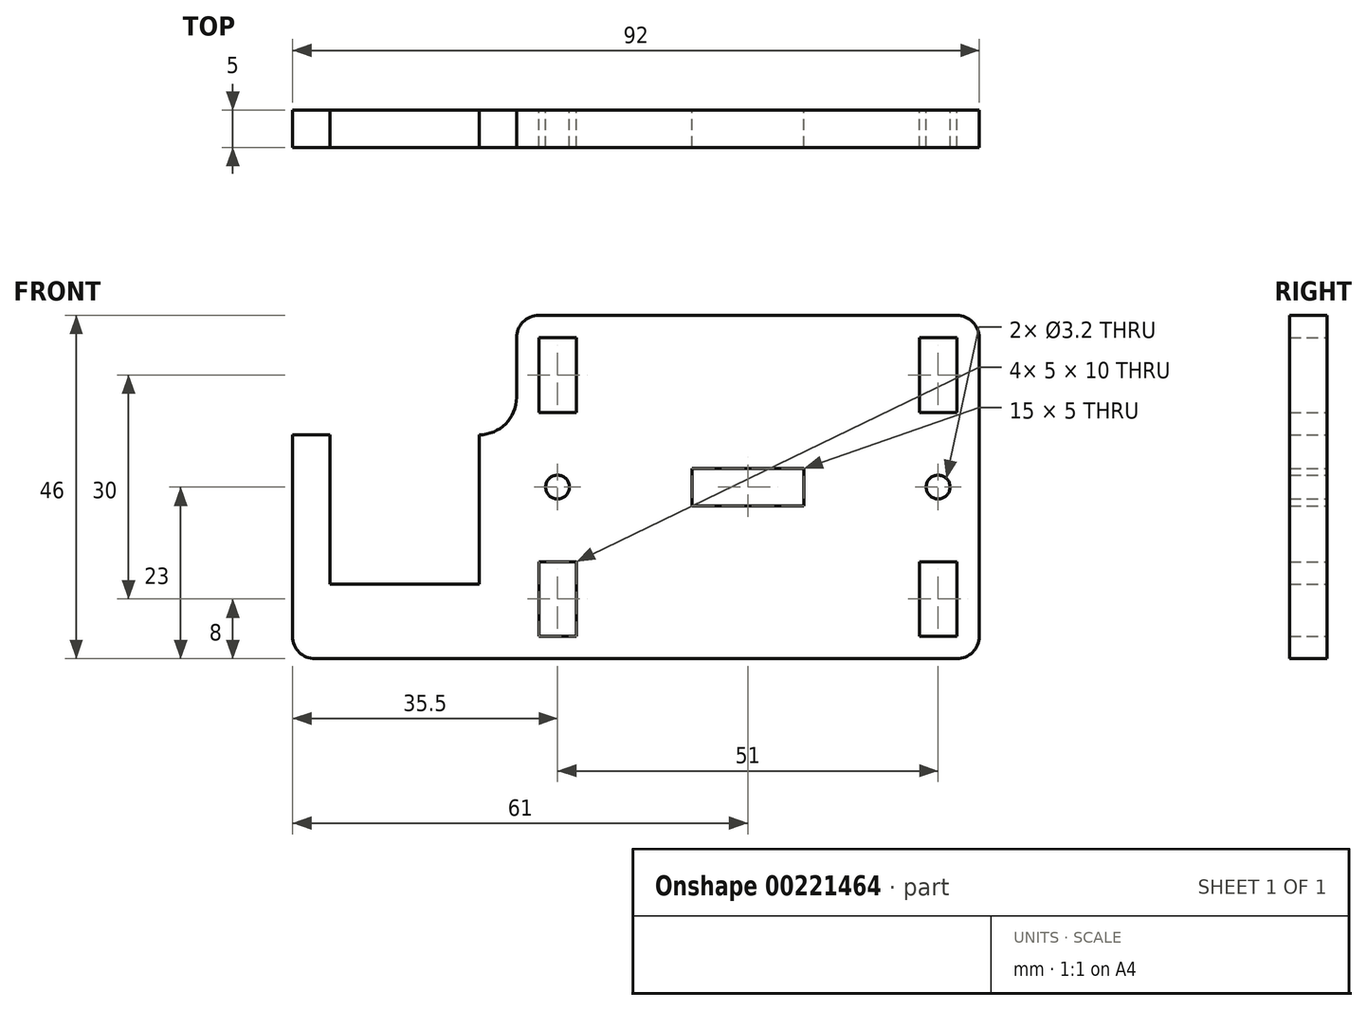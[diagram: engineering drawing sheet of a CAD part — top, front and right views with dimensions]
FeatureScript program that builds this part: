
annotation { "Feature Type Name" : "Feature", "Feature Type Description" : "" }
export const myFeature = defineFeature(function(context is Context, id is Id, definition is map)
    precondition{}
    {
        {
            assignVariable(context, id + "F0", {"name" : "thickness", "anyValue" : 5 * mm});
        }
        {
            var Q0;
            Q0=qCreatedBy(makeId("Front.planeOp"),FACE);
            var sketch = newSketch(context, id + "F1", { "sketchPlane" : qUnion([Q0])});
            skLineSegment(sketch, "E0.bottom", {"start": v(0, 0) * mm, "end": v(20, 0) * mm, "construction": true});
            skLineSegment(sketch, "E0.top", {"start": v(0, 30) * mm, "end": v(20, 30) * mm, "construction": true});
            skLineSegment(sketch, "E0.left", {"start": v(0, 0) * mm, "end": v(0, 30) * mm, "construction": true});
            skLineSegment(sketch, "E0.right", {"start": v(20, 0) * mm, "end": v(20, 30) * mm, "construction": true});
            skLineSegment(sketch, "E1.bottom", {"start": v(2.5, 20) * mm, "end": v(17.5, 20) * mm, "construction": true});
            skLineSegment(sketch, "E1.top", {"start": v(2.5, 10) * mm, "end": v(17.5, 10) * mm, "construction": true});
            skLineSegment(sketch, "E1.left", {"start": v(2.5, 20) * mm, "end": v(2.5, 10) * mm, "construction": true});
            skLineSegment(sketch, "E1.right", {"start": v(17.5, 20) * mm, "end": v(17.5, 10) * mm, "construction": true});
            skPoint(sketch, "E2", {"position": v(10, 30) * mm});
            skPoint(sketch, "E3", {"position": v(10, 20) * mm});
            skPoint(sketch, "E4", {"position": v(2.5, 15) * mm});
            skPoint(sketch, "E5", {"position": v(0, 15) * mm});
            skLineSegment(sketch, "E6.0", {"start": v(-21, 27) * mm, "end": v(-21, 35) * mm});
            skLineSegment(sketch, "E6.2", {"start": v(41, -5) * mm, "end": v(41, 35) * mm});
            skLineSegment(sketch, "E7.bottom", {"start": v(-18, 35) * mm, "end": v(-13, 35) * mm});
            skLineSegment(sketch, "E7.top", {"start": v(-18, 25) * mm, "end": v(-13, 25) * mm});
            skLineSegment(sketch, "E7.left", {"start": v(-18, 35) * mm, "end": v(-18, 25) * mm});
            skLineSegment(sketch, "E7.right", {"start": v(-13, 35) * mm, "end": v(-13, 25) * mm});
            skLineSegment(sketch, "E8", {"start": v(-21, 15) * mm, "end": v(41, 15) * mm, "construction": true});
            skLineSegment(sketch, "E9.MirrorCS", {"start": v(-18, -5) * mm, "end": v(-18, 5) * mm});
            skLineSegment(sketch, "E10.MirrorCS", {"start": v(-18, -5) * mm, "end": v(-13, -5) * mm});
            skLineSegment(sketch, "E11.MirrorCS", {"start": v(-13, -5) * mm, "end": v(-13, 5) * mm});
            skLineSegment(sketch, "E12.MirrorCS", {"start": v(-18, 5) * mm, "end": v(-13, 5) * mm});
            skLineSegment(sketch, "E13", {"start": v(10, 38) * mm, "end": v(10, -8) * mm, "construction": true});
            skLineSegment(sketch, "E14.MirrorCS", {"start": v(38, 35) * mm, "end": v(33, 35) * mm});
            skLineSegment(sketch, "E15.MirrorCS", {"start": v(38, 35) * mm, "end": v(38, 25) * mm});
            skLineSegment(sketch, "E16.MirrorCS", {"start": v(33, 35) * mm, "end": v(33, 25) * mm});
            skLineSegment(sketch, "E17.MirrorCS", {"start": v(38, 25) * mm, "end": v(33, 25) * mm});
            skLineSegment(sketch, "E18.MirrorCS", {"start": v(38, -5) * mm, "end": v(38, 5) * mm});
            skLineSegment(sketch, "E19.MirrorCS", {"start": v(38, 5) * mm, "end": v(33, 5) * mm});
            skLineSegment(sketch, "E20.MirrorCS", {"start": v(33, -5) * mm, "end": v(33, 5) * mm});
            skLineSegment(sketch, "E21.MirrorCS", {"start": v(38, -5) * mm, "end": v(33, -5) * mm});
            skCircle(sketch, "E22", {"center": v(-15.5, 15) * mm, "radius": 1.6 * mm});
            skPoint(sketch, "E23", {"position": v(-15.5, 25) * mm});
            skCircle(sketch, "E24.MirrorC", {"center": v(35.5, 15) * mm, "radius": 1.6 * mm});
            skLineSegment(sketch, "E25.bottom", {"start": v(2.5, 17.5) * mm, "end": v(17.5, 17.5) * mm});
            skLineSegment(sketch, "E25.top", {"start": v(2.5, 12.5) * mm, "end": v(17.5, 12.5) * mm});
            skLineSegment(sketch, "E25.left", {"start": v(2.5, 17.5) * mm, "end": v(2.5, 12.5) * mm});
            skLineSegment(sketch, "E25.right", {"start": v(17.5, 17.5) * mm, "end": v(17.5, 12.5) * mm});
            skPoint(sketch, "E26", {"position": v(10, 17.5) * mm});
            skLineSegment(sketch, "E27", {"start": v(-18, 38) * mm, "end": v(38, 38) * mm});
            skLineSegment(sketch, "E28", {"start": v(-48, -8) * mm, "end": v(38, -8) * mm});
            skPoint(sketch, "E29.visualSharp", {"position": v(-21, 38) * mm});
            skArc(sketch, "E29.filletArc", {"start": v(-18, 38) * mm, "mid": v(-20.12, 37.12) * mm, "end": v(-21, 35) * mm});
            skPoint(sketch, "E30.visualSharp", {"position": v(41, 38) * mm});
            skArc(sketch, "E30.filletArc", {"start": v(41, 35) * mm, "mid": v(40.12, 37.12) * mm, "end": v(38, 38) * mm});
            skPoint(sketch, "E31.visualSharp", {"position": v(-21, -8) * mm});
            skPoint(sketch, "E32.visualSharp", {"position": v(41, -8) * mm});
            skArc(sketch, "E32.filletArc", {"start": v(38, -8) * mm, "mid": v(40.12, -7.12) * mm, "end": v(41, -5) * mm});
            skLineSegment(sketch, "E33", {"start": v(-51, 22) * mm, "end": v(-51, -5) * mm});
            skLineSegment(sketch, "E34.0", {"start": v(-46, 2) * mm, "end": v(-26, 2) * mm});
            skLineSegment(sketch, "E34.1", {"start": v(-46, 22) * mm, "end": v(-46, 2) * mm});
            skLineSegment(sketch, "E35", {"start": v(-26, 22) * mm, "end": v(-26, 2) * mm});
            skPoint(sketch, "E36.visualSharp", {"position": v(-51, -8) * mm});
            skArc(sketch, "E36.filletArc", {"start": v(-51, -5) * mm, "mid": v(-50.12, -7.12) * mm, "end": v(-48, -8) * mm});
            skPoint(sketch, "E37.visualSharp", {"position": v(-21, 22) * mm});
            skArc(sketch, "E37.filletArc", {"start": v(-26, 22) * mm, "mid": v(-22.46, 23.46) * mm, "end": v(-21, 27) * mm});
            skLineSegment(sketch, "E38", {"start": v(-46, 22) * mm, "end": v(-51, 22) * mm});
            skSolve(sketch);
        }
        {
            var Q0;
            Q0=qSketchRegion(id+"F1",true);
            extrude(context, id + "F2", {"entities" : qUnion([Q0]), "depth" : getVariable(context, 'thickness')});
        }
    });
